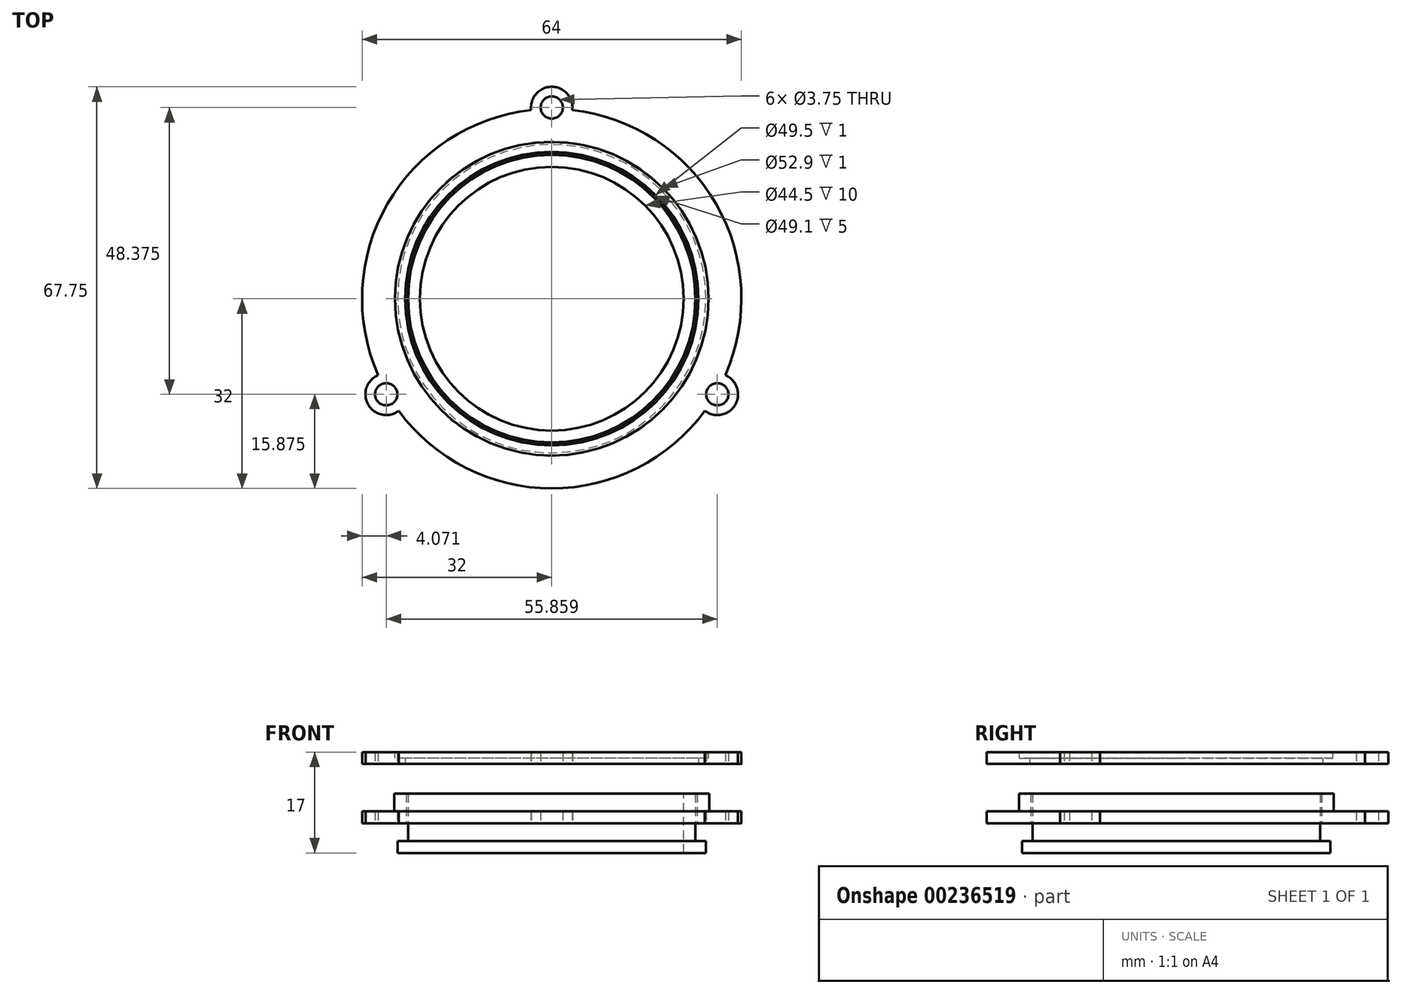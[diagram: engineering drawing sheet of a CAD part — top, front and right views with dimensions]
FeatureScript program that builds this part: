
annotation { "Feature Type Name" : "Feature", "Feature Type Description" : "" }
export const myFeature = defineFeature(function(context is Context, id is Id, definition is map)
    precondition{}
    {
        {
            var Q0;
            Q0=qCreatedBy(makeId("Top.planeOp"),FACE);
            var sketch = newSketch(context, id + "F0", { "sketchPlane" : qUnion([Q0])});
            skCircle(sketch, "E0", {"center": v(0, 0) * mm, "radius": 26 * mm});
            skSolve(sketch);
        }
        {
            var Q0;
            Q0=makeQuery(id+"F0.imprint","IMPRINT",FACE,{"disambiguationData":[TD([[makeQuery(id+"F0.imprint","IMPRINT",EDGE,{"derivedFrom":sQuery(id+"F0.wireOp",EDGE,"E0")}),1.0]])]});
            extrude(context, id + "F1", {"entities" : qUnion([Q0]), "depth" : 2 * mm});
        }
        {
            var Q0;
            Q0=makeQuery(id+"F1.opExtrude","CAP_FACE",FACE,{"disambiguationData":[OSD([sQuery(id+"F0.wireOp",EDGE,"E0")])],"isStart":false});
            var sketch = newSketch(context, id + "F2", { "sketchPlane" : qUnion([Q0])});
            skCircle(sketch, "E1", {"center": v(0, 0) * mm, "radius": 22.25 * mm});
            skSolve(sketch);
        }
        {
            var Q0;
            Q0=makeQuery(id+"F2.imprint","IMPRINT",FACE,{"disambiguationData":[TD([[makeQuery(id+"F2.imprint","IMPRINT",EDGE,{"derivedFrom":sQuery(id+"F2.wireOp",EDGE,"E1")}),1.0]])]});
            extrude(context, id + "F3", {"entities" : qUnion([Q0]), "operationType" : NewBodyOperationType.REMOVE, "oppositeDirection" : true, "depth" : 25 * mm});
        }
        {
            var Q0;
            Q0=makeQuery(id+"F1.opExtrude","CAP_FACE",FACE,{"disambiguationData":[OSD([sQuery(id+"F0.wireOp",EDGE,"E0")])],"isStart":false});
            var sketch = newSketch(context, id + "F4", { "sketchPlane" : qUnion([Q0])});
            skPoint(sketch, "E2", {"position": v(-4.35, 21.82) * mm});
            skCircle(sketch, "E3", {"center": v(0, 0) * mm, "radius": 22.25 * mm});
            skCircle(sketch, "E4", {"center": v(0, 0) * mm, "radius": 24.25 * mm});
            skSolve(sketch);
        }
        {
            var Q0;
            Q0 = qSketchRegion(id + "F4", true);
            extrude(context, id + "F5", {"entities" : qUnion([Q0]), "operationType" : NewBodyOperationType.ADD, "depth" : 8 * mm});
        }
        {
            var Q0;
            Q0=qCreatedBy(makeId("Top.planeOp"),FACE);
            cPlane(context, id + "F6", {"entities" : qUnion([Q0]), "cplaneType" : CPlaneType.OFFSET, "offset" : 5 * mm, "width" : 150 * mm, "height" : 150 * mm});
        }
        {
            var Q0;
            Q0=qCreatedBy(id+"F6.planeOp",FACE);
            var sketch = newSketch(context, id + "F7", { "sketchPlane" : qUnion([Q0])});
            skCircle(sketch, "E5", {"center": v(0, 0) * mm, "radius": 24.55 * mm});
            skCircle(sketch, "E6", {"center": v(0, 0) * mm, "radius": 29 * mm, "construction": true});
            skCircle(sketch, "E7", {"center": v(0, 0) * mm, "radius": 29.5 * mm, "construction": true});
            skCircle(sketch, "E8", {"center": v(0, 32.25) * mm, "radius": 2.75 * mm, "construction": true});
            skCircle(sketch, "E9", {"center": v(-27.93, -16.12) * mm, "radius": 2.75 * mm, "construction": true});
            skCircle(sketch, "E10", {"center": v(27.93, -16.12) * mm, "radius": 2.75 * mm, "construction": true});
            skLineSegment(sketch, "E11", {"start": v(0, 32.25) * mm, "end": v(0, 0) * mm, "construction": true});
            skLineSegment(sketch, "E12", {"start": v(0, 0) * mm, "end": v(-27.93, -16.12) * mm, "construction": true});
            skLineSegment(sketch, "E13", {"start": v(0, 0) * mm, "end": v(27.93, -16.12) * mm, "construction": true});
            skArc(sketch, "E14", {"start": v(-29.29, -12.9) * mm, "mid": v(-27.71, 16) * mm, "end": v(-3.47, 31.81) * mm});
            skArc(sketch, "E15", {"start": v(3.47, 31.81) * mm, "mid": v(27.71, 16) * mm, "end": v(29.29, -12.9) * mm});
            skArc(sketch, "E16", {"start": v(-25.81, -18.91) * mm, "mid": v(0, -32) * mm, "end": v(25.81, -18.91) * mm});
            skArc(sketch, "E17", {"start": v(-3.47, 31.81) * mm, "mid": v(0, 35.75) * mm, "end": v(3.47, 31.81) * mm});
            skArc(sketch, "E18", {"start": v(29.29, -12.9) * mm, "mid": v(30.96, -17.87) * mm, "end": v(25.81, -18.91) * mm});
            skArc(sketch, "E19", {"start": v(-29.29, -12.9) * mm, "mid": v(-30.96, -17.87) * mm, "end": v(-25.81, -18.91) * mm});
            skCircle(sketch, "E20", {"center": v(-27.93, -16.12) * mm, "radius": 1.88 * mm});
            skCircle(sketch, "E21", {"center": v(0, 32.25) * mm, "radius": 1.88 * mm});
            skCircle(sketch, "E22", {"center": v(27.93, -16.12) * mm, "radius": 1.88 * mm});
            skSolve(sketch);
        }
        {
            var Q0;
            Q0=makeQuery(id+"F7.imprint","IMPRINT",FACE,{"disambiguationData":[TD([[makeQuery(id+"F7.imprint","IMPRINT",EDGE,{"derivedFrom":sQuery(id+"F7.wireOp",EDGE,"E5")}),-1.0]])]});
            extrude(context, id + "F8", {"entities" : qUnion([Q0]), "depth" : 2 * mm});
        }
        {
            var Q0;
            Q0=makeQuery(id+"F8.opExtrude","CAP_FACE",FACE,{"disambiguationData":[OSD([sQuery(id+"F7.wireOp",EDGE,"E5"),sQuery(id+"F7.wireOp",EDGE,"E14"),sQuery(id+"F7.wireOp",EDGE,"E15"),sQuery(id+"F7.wireOp",EDGE,"E16"),sQuery(id+"F7.wireOp",EDGE,"E17"),sQuery(id+"F7.wireOp",EDGE,"E18"),sQuery(id+"F7.wireOp",EDGE,"E19"),sQuery(id+"F7.wireOp",EDGE,"E20"),sQuery(id+"F7.wireOp",EDGE,"E21"),sQuery(id+"F7.wireOp",EDGE,"E22")])],"isStart":false});
            var sketch = newSketch(context, id + "F9", { "sketchPlane" : qUnion([Q0])});
            skCircle(sketch, "E23", {"center": v(0, 0) * mm, "radius": 24.55 * mm});
            skPoint(sketch, "E24", {"position": v(-12.55, 21.1) * mm});
            skCircle(sketch, "E25", {"center": v(0, 0) * mm, "radius": 26.55 * mm});
            skSolve(sketch);
        }
        {
            var Q0;
            Q0 = qSketchRegion(id + "F9", true);
            extrude(context, id + "F10", {"entities" : qUnion([Q0]), "operationType" : NewBodyOperationType.ADD, "depth" : 3 * mm});
        }
        {
            var Q0;
            Q0=qCreatedBy(makeId("Top.planeOp"),FACE);
            cPlane(context, id + "F11", {"entities" : qUnion([Q0]), "cplaneType" : CPlaneType.OFFSET, "offset" : 15 * mm, "width" : 150 * mm, "height" : 150 * mm});
        }
        {
            var Q0;
            Q0=qCreatedBy(id+"F11.planeOp",FACE);
            var sketch = newSketch(context, id + "F12", { "sketchPlane" : qUnion([Q0])});
            skCircle(sketch, "E26", {"center": v(0, 0) * mm, "radius": 29.5 * mm, "construction": true});
            skCircle(sketch, "E27", {"center": v(0, 32.25) * mm, "radius": 2.75 * mm, "construction": true});
            skCircle(sketch, "E28", {"center": v(-27.93, -16.12) * mm, "radius": 2.75 * mm, "construction": true});
            skCircle(sketch, "E29", {"center": v(27.93, -16.12) * mm, "radius": 2.75 * mm, "construction": true});
            skLineSegment(sketch, "E30", {"start": v(0, 32.25) * mm, "end": v(0, 0) * mm, "construction": true});
            skLineSegment(sketch, "E31", {"start": v(0, 0) * mm, "end": v(27.93, -16.12) * mm, "construction": true});
            skLineSegment(sketch, "E32", {"start": v(0, 0) * mm, "end": v(-27.93, -16.13) * mm, "construction": true});
            skCircle(sketch, "E33", {"center": v(0, 32.25) * mm, "radius": 1.88 * mm});
            skCircle(sketch, "E34", {"center": v(27.93, -16.12) * mm, "radius": 1.88 * mm});
            skCircle(sketch, "E35", {"center": v(-27.93, -16.12) * mm, "radius": 1.88 * mm});
            skArc(sketch, "E36", {"start": v(-29.29, -12.9) * mm, "mid": v(-27.71, 16) * mm, "end": v(-3.47, 31.81) * mm});
            skArc(sketch, "E37", {"start": v(3.47, 31.81) * mm, "mid": v(27.71, 16) * mm, "end": v(29.29, -12.9) * mm});
            skArc(sketch, "E38", {"start": v(-25.81, -18.91) * mm, "mid": v(0, -32) * mm, "end": v(25.81, -18.91) * mm});
            skArc(sketch, "E39", {"start": v(-29.29, -12.9) * mm, "mid": v(-30.96, -17.88) * mm, "end": v(-25.81, -18.91) * mm});
            skArc(sketch, "E40", {"start": v(25.81, -18.91) * mm, "mid": v(30.96, -17.87) * mm, "end": v(29.29, -12.9) * mm});
            skArc(sketch, "E41", {"start": v(-3.47, 31.81) * mm, "mid": v(0, 35.75) * mm, "end": v(3.47, 31.81) * mm});
            skCircle(sketch, "E42", {"center": v(0, 0) * mm, "radius": 24.75 * mm});
            skSolve(sketch);
        }
        {
            var Q0;
            Q0 = qSketchRegion(id + "F12", true);
            extrude(context, id + "F13", {"entities" : qUnion([Q0]), "depth" : 2 * mm});
        }
        {
            var Q0;
            Q0=makeQuery(id+"F13.opExtrude","CAP_FACE",FACE,{"disambiguationData":[OSD([sQuery(id+"F12.wireOp",EDGE,"E33"),sQuery(id+"F12.wireOp",EDGE,"E34"),sQuery(id+"F12.wireOp",EDGE,"E35"),sQuery(id+"F12.wireOp",EDGE,"E36"),sQuery(id+"F12.wireOp",EDGE,"E37"),sQuery(id+"F12.wireOp",EDGE,"E38"),sQuery(id+"F12.wireOp",EDGE,"E39"),sQuery(id+"F12.wireOp",EDGE,"E40"),sQuery(id+"F12.wireOp",EDGE,"E41"),sQuery(id+"F12.wireOp",EDGE,"E42")])],"isStart":false});
            var sketch = newSketch(context, id + "F14", { "sketchPlane" : qUnion([Q0])});
            skCircle(sketch, "E43", {"center": v(0, 0) * mm, "radius": 26.45 * mm});
            skSolve(sketch);
        }
        {
            var Q0;
            Q0=makeQuery(id+"F14.imprint","IMPRINT",FACE,{"disambiguationData":[TD([[makeQuery(id+"F14.imprint","IMPRINT",EDGE,{"derivedFrom":sQuery(id+"F14.wireOp",EDGE,"E43")}),1.0]])]});
            extrude(context, id + "F15", {"entities" : qUnion([Q0]), "operationType" : NewBodyOperationType.REMOVE, "oppositeDirection" : true, "depth" : 1 * mm});
        }
    });
